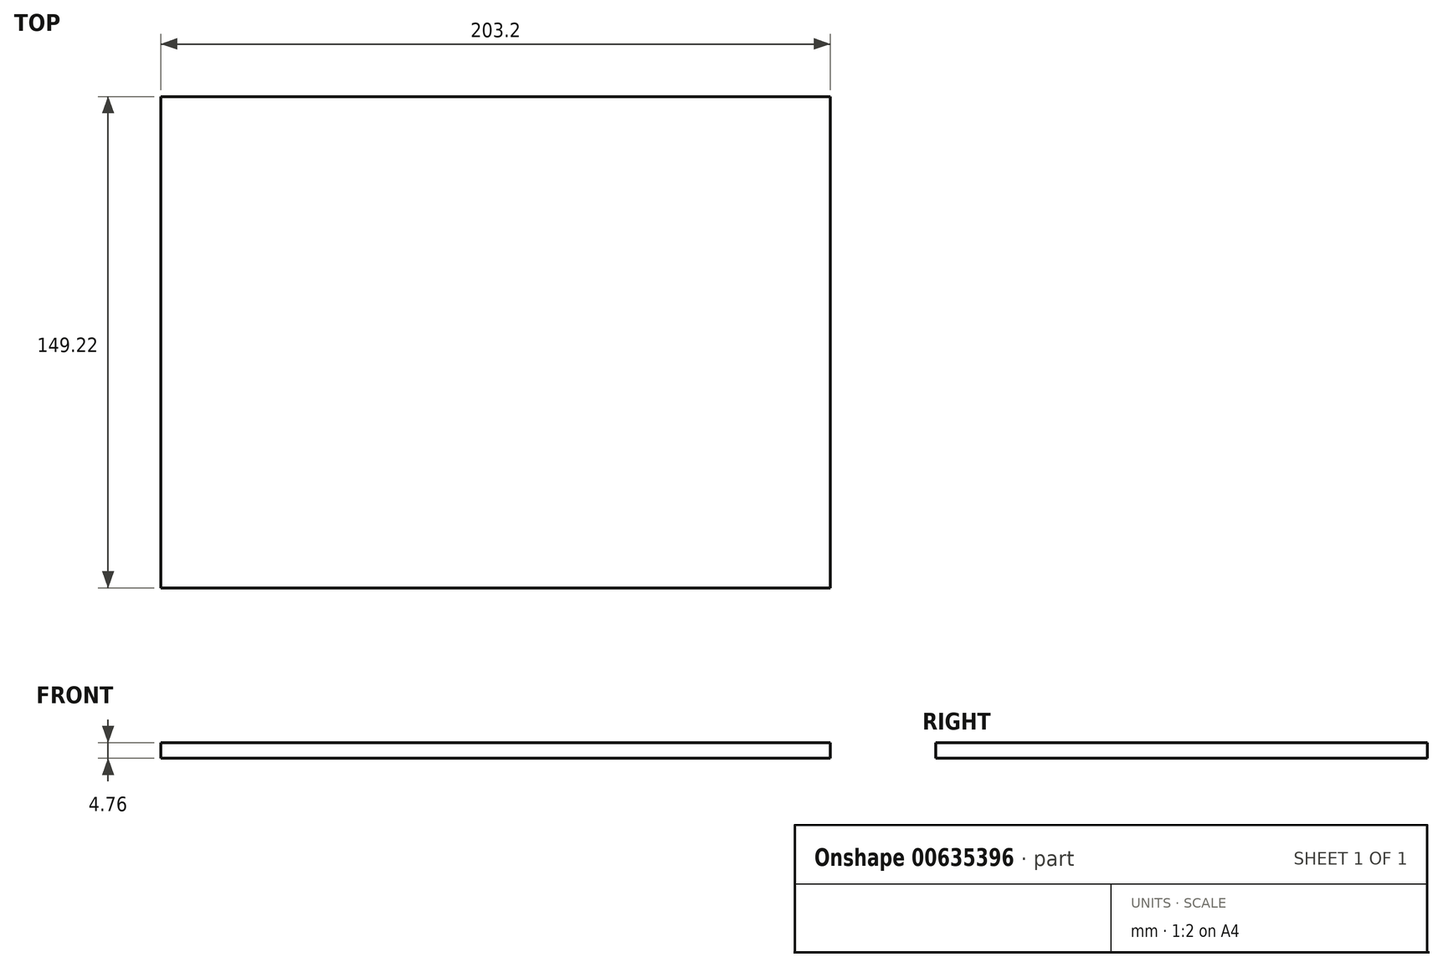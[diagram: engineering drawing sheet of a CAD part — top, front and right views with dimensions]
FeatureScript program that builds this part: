
annotation { "Feature Type Name" : "Feature", "Feature Type Description" : "" }
export const myFeature = defineFeature(function(context is Context, id is Id, definition is map)
    precondition{}
    {
        {
            var Q0;
            Q0=qCreatedBy(makeId("Top.planeOp"),FACE);
            var sketch = newSketch(context, id + "F0", { "sketchPlane" : qUnion([Q0])});
            skLineSegment(sketch, "E0.bottom", {"start": v(-101.6, 74.61) * mm, "end": v(101.6, 74.61) * mm});
            skLineSegment(sketch, "E0.top", {"start": v(-101.6, -74.61) * mm, "end": v(101.6, -74.61) * mm});
            skLineSegment(sketch, "E0.left", {"start": v(-101.6, 74.61) * mm, "end": v(-101.6, -74.61) * mm});
            skLineSegment(sketch, "E0.right", {"start": v(101.6, 74.61) * mm, "end": v(101.6, -74.61) * mm});
            skPoint(sketch, "E0.middle", {"position": v(0, 0) * mm});
            skSolve(sketch);
        }
        {
            var Q0;
            Q0=qSketchRegion(id+"F0",true);
            extrude(context, id + "F1", {"entities" : qUnion([Q0]), "depth" : 4.76 * mm});
        }
    });
